# Revit family: PRD_AR_ShwrHds_ShowerHead_AQUA751_AQUA754-5_AQUA757
name_source: partatom
category: Plumbing Fixtures
revit_build: Autodesk Revit 2018 (Build: 20190510_1515(x64)
units: mm (PartAtom-declared; Revit-internal decimal feet)

## family parameters
Cut with Voids When Loaded = Yes
Host = Face
OmniClass Number = 23.45.55.14
OmniClass Title = Single Faucets
Part Type = Normal
Room Calculation Point = No
Round Connector Dimension = Use Diameter
Shared = No

## types (4) — shared parameters
AssetType = Fixed
BodyMaterial = PRD_AR_Steel
Category = Pr_40_20_87_76, Shower heads
Color = Chrome
Default Elevation = 2100 mm
DiameterNominal = 15  [stored 0.0492126 ft]
DurationUnit = year
Finish = Chrome
HasTray = No
IfcExportAs = IfcSanitaryTerminalType
IfcExportType = SHOWER
InletSize = DN 15 (1/2 inch.)
Manufacturer = KWC Group AG
ManufacturerName = KWC Group AG
ManufacturerURL = www.kwc.com
NBSDescription = Shower heads
NBSReference = 45-35-70/333
NominalWidth = 59 mm
ProductInformation = https://pim.kwc.com
ShowerHeadMaterial = PRD_AR_ChromatedBrass_HighPolished
ShowerType = Other
URL = www.kwc.com
Uniclass2015Code = Pr_40_20_87_76
Uniclass2015Title = Shower heads
Uniclass2015Version = Products v1.10
Version = 1
WarrantyDurationUnit = year
zero-valued in all types: DrainSize, MaterialThickness

## per-type parameters (varying)
| type | AQUA751-756 | AQUA757 | BIMObjectName | Description | FlowColdWater | GrossWeight | Model | ModelNumber | ModelReference | Name | NetWeight | NominalDepth | NominalHeight | NominalLength | Size |
| AQUA754 - 0,1 l/s | Yes | No | PRD_AR_ShowerHeads_ShowerHead_AQUA754 | AQUAJET-Slimline shower head DN 15 with plastic jet face with anti-calcification system and low aerosol formation, jet angle 16°, for wall connection, polished chromium-plated brass. with flow controller 0.10 l/s | 0.1 L/s | 0.57 kg | AQUA754 | 2000102683 | AQUA754 | Shower head AQUA754 | 0.52 kg | 83 mm  [stored 0.27231 ft] | 59 mm | 70 mm  [stored 0.229659 ft] | 83 x 70 x 59 mm |
| AQUA755 - 0,15 l/s | Yes | No | PRD_AR_ShowerHeads_ShowerHead_AQUA755 | AQUAJET-Slimline shower head DN 15 with plastic jet face with anti-calcification system and low aerosol formation, jet angle 16°, for wall connection, polished chromium-plated brass. flow controller 0.15 l/s | 0.2 L/s | 0.57 kg | AQUA755 | 2000102684 | AQUA755 | Shower head AQUA755 | 0.52 kg | 83 mm  [stored 0.27231 ft] | 59 mm | 70 mm  [stored 0.229659 ft] | 83 x 70 x 59 mm |
| AQUA757 | No | Yes | PRD_AR_ShowerHeads_ShowerHead_AQUA757 | AQUAJET-Slimline shower head DN 15 with plastic jet face with anti-calcification system and low aerosol formation, for surface pipe mounting, polished chromium-plated brass. With flow controllers 0.15 l/s and 0.20 l/s. | 0.3 L/s | 0.92 kg | AQUA757 | 2000103757 | AQUA757 | Shower head AQUA757 | 0.87 kg | 108 mm  [stored 0.354331 ft] | 72 mm  [stored 0.23622 ft] | 80 mm  [stored 0.262467 ft] | 108 x 80 x 72 mm |
| AQUA751 - 0,15 l/s | Yes | No | PRD_AR_ShowerHeads_ShowerHead_AQUA751 | AQUAJET-Slimline shower head DN 15 with plastic jet face with anti-calcification system and low aerosol formation, for wall connection, polished chromium-plated brass. with flow control 0,15 l/s | 0.2 L/s | 0.67 kg | AQUA751 | 2000065932 | AQUA751 | Shower head AQUA751 | 0.64 kg | 83 mm  [stored 0.27231 ft] | 59 mm | 70 mm  [stored 0.229659 ft] | 83 x 70 x 59 mm |

note: [stored X ft] marks values corroborated as IEEE doubles in the binary element streams (Revit-internal decimal feet)

## geometry (parser evidence)
native form markers: Sweep x15
no freeform markers — native parametric forms only
